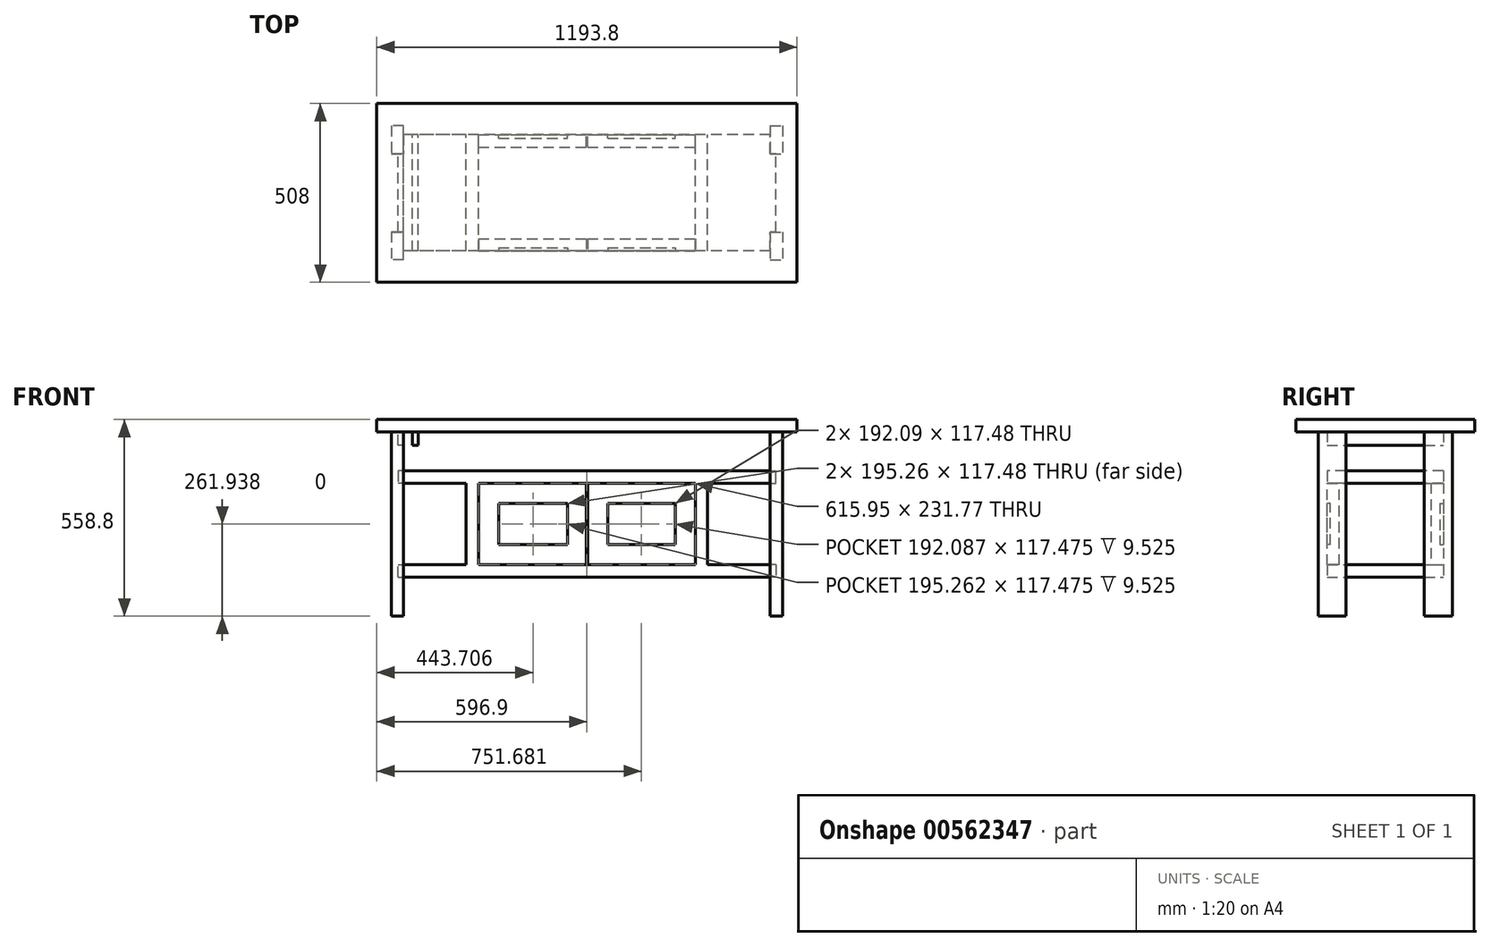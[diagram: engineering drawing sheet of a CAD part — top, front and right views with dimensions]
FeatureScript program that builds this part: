
annotation { "Feature Type Name" : "Feature", "Feature Type Description" : "" }
export const myFeature = defineFeature(function(context is Context, id is Id, definition is map)
    precondition{}
    {
        {
            var Q0;
            Q0=qCreatedBy(makeId("Front.planeOp"),FACE);
            var sketch = newSketch(context, id + "F0", { "sketchPlane" : qUnion([Q0])});
            skLineSegment(sketch, "E0.bottom", {"start": v(596.9, 558.8) * mm, "end": v(-596.9, 558.8) * mm});
            skLineSegment(sketch, "E0.top", {"start": v(596.9, 523.88) * mm, "end": v(-596.9, 523.88) * mm});
            skLineSegment(sketch, "E0.left", {"start": v(596.9, 558.8) * mm, "end": v(596.9, 523.88) * mm});
            skLineSegment(sketch, "E0.right", {"start": v(-596.9, 558.8) * mm, "end": v(-596.9, 523.88) * mm});
            skPoint(sketch, "E0.middle", {"position": v(0, 541.34) * mm});
            skLineSegment(sketch, "E1.bottom", {"start": v(536.58, 146.05) * mm, "end": v(342.9, 146.05) * mm});
            skLineSegment(sketch, "E1.top", {"start": v(536.58, 111.13) * mm, "end": v(-536.58, 111.12) * mm});
            skLineSegment(sketch, "E1.left", {"start": v(536.58, 146.05) * mm, "end": v(536.58, 111.13) * mm});
            skLineSegment(sketch, "E1.right", {"start": v(-536.58, 146.05) * mm, "end": v(-536.58, 111.12) * mm});
            skPoint(sketch, "E1.middle", {"position": v(0, 128.59) * mm});
            skLineSegment(sketch, "E2", {"start": v(307.98, 146.05) * mm, "end": v(307.98, 377.83) * mm});
            skLineSegment(sketch, "E3", {"start": v(342.9, 377.82) * mm, "end": v(342.9, 146.05) * mm});
            skLineSegment(sketch, "E4", {"start": v(0, 0) * mm, "end": v(0, -191.79) * mm, "construction": true});
            skLineSegment(sketch, "E5.MirrorCS", {"start": v(-342.9, 377.82) * mm, "end": v(-342.9, 146.05) * mm});
            skLineSegment(sketch, "E6.MirrorCS", {"start": v(-307.98, 146.05) * mm, "end": v(-307.98, 377.83) * mm});
            skLineSegment(sketch, "E7.trimOffspring", {"start": v(307.98, 146.05) * mm, "end": v(-307.98, 146.05) * mm});
            skLineSegment(sketch, "E8.trimOffspring", {"start": v(-342.9, 146.05) * mm, "end": v(-536.58, 146.05) * mm});
            skLineSegment(sketch, "E9.bottom", {"start": v(-536.58, 377.83) * mm, "end": v(-342.9, 377.83) * mm});
            skLineSegment(sketch, "E9.top", {"start": v(-536.58, 412.75) * mm, "end": v(536.57, 412.75) * mm});
            skLineSegment(sketch, "E9.left", {"start": v(-536.58, 377.83) * mm, "end": v(-536.58, 412.75) * mm});
            skLineSegment(sketch, "E9.right", {"start": v(536.58, 377.83) * mm, "end": v(536.58, 412.75) * mm});
            skLineSegment(sketch, "E10.trimOffspring", {"start": v(-307.98, 377.83) * mm, "end": v(307.97, 377.83) * mm});
            skLineSegment(sketch, "E11.trimOffspring", {"start": v(342.9, 377.83) * mm, "end": v(536.57, 377.83) * mm});
            skLineSegment(sketch, "E12", {"start": v(-342.9, 377.83) * mm, "end": v(-307.98, 377.83) * mm, "construction": true});
            skLineSegment(sketch, "E13.bottom", {"start": v(536.57, 523.88) * mm, "end": v(520.7, 523.88) * mm});
            skLineSegment(sketch, "E13.top", {"start": v(536.57, 485.78) * mm, "end": v(520.7, 485.78) * mm});
            skLineSegment(sketch, "E13.left", {"start": v(536.57, 523.88) * mm, "end": v(536.57, 485.78) * mm});
            skLineSegment(sketch, "E13.right", {"start": v(520.7, 523.88) * mm, "end": v(520.7, 485.78) * mm});
            skLineSegment(sketch, "E14.bottom", {"start": v(495.3, 523.88) * mm, "end": v(479.43, 523.88) * mm});
            skLineSegment(sketch, "E14.top", {"start": v(495.3, 485.78) * mm, "end": v(479.43, 485.78) * mm});
            skLineSegment(sketch, "E14.left", {"start": v(495.3, 523.88) * mm, "end": v(495.3, 485.78) * mm});
            skLineSegment(sketch, "E14.right", {"start": v(479.43, 523.88) * mm, "end": v(479.43, 485.78) * mm});
            skLineSegment(sketch, "E15.MirrorCS", {"start": v(-520.7, 523.88) * mm, "end": v(-520.7, 485.77) * mm});
            skLineSegment(sketch, "E16.MirrorCS", {"start": v(-495.3, 485.78) * mm, "end": v(-479.43, 485.78) * mm});
            skLineSegment(sketch, "E17.MirrorCS", {"start": v(-536.58, 485.77) * mm, "end": v(-520.7, 485.77) * mm});
            skLineSegment(sketch, "E18.MirrorCS", {"start": v(-495.3, 523.88) * mm, "end": v(-495.3, 485.77) * mm});
            skLineSegment(sketch, "E19.MirrorCS", {"start": v(-479.43, 523.88) * mm, "end": v(-479.43, 485.77) * mm});
            skLineSegment(sketch, "E20.MirrorCS", {"start": v(-536.57, 523.88) * mm, "end": v(-520.7, 523.88) * mm});
            skLineSegment(sketch, "E21.MirrorCS", {"start": v(-536.57, 523.88) * mm, "end": v(-536.57, 485.77) * mm});
            skLineSegment(sketch, "E22.MirrorCS", {"start": v(-495.3, 523.88) * mm, "end": v(-479.43, 523.88) * mm});
            skSolve(sketch);
        }
        {
            var Q0;
            Q0=makeQuery(id+"F0.imprint","IMPRINT",FACE,{"disambiguationData":[TD([[makeQuery(id+"F0.imprint","IMPRINT",EDGE,{"derivedFrom":sQuery(id+"F0.wireOp",EDGE,"E0.bottom")}),1.0]])]});
            extrude(context, id + "F1", {"entities" : qUnion([Q0]), "endBound" : BoundingType.SYMMETRIC, "depth" : 508 * mm, "offsetDistance" : 25.4 * mm});
        }
        {
            var Q0;
            Q0=makeQuery(id+"F0.imprint","IMPRINT",FACE,{"disambiguationData":[TD([[makeQuery(id+"F0.imprint","IMPRINT",EDGE,{"derivedFrom":sQuery(id+"F0.wireOp",EDGE,"E1.bottom")}),1.0]])]});
            var Q1;
            Q1=makeQuery(id+"F0.imprint","IMPRINT",FACE,{"disambiguationData":[TD([[makeQuery(id+"F0.imprint","IMPRINT",EDGE,{"derivedFrom":sQuery(id+"F0.wireOp",EDGE,"E13.bottom")}),1.0]])]});
            var Q2;
            Q2=makeQuery(id+"F0.imprint","IMPRINT",FACE,{"disambiguationData":[TD([[makeQuery(id+"F0.imprint","IMPRINT",EDGE,{"derivedFrom":sQuery(id+"F0.wireOp",EDGE,"E14.bottom")}),1.0]])]});
            var Q3;
            Q3=makeQuery(id+"F0.imprint","IMPRINT",FACE,{"disambiguationData":[TD([[makeQuery(id+"F0.imprint","IMPRINT",EDGE,{"derivedFrom":sQuery(id+"F0.wireOp",EDGE,"E16.MirrorCS")}),1.0]])]});
            var Q4;
            Q4=makeQuery(id+"F0.imprint","IMPRINT",FACE,{"disambiguationData":[TD([[makeQuery(id+"F0.imprint","IMPRINT",EDGE,{"derivedFrom":sQuery(id+"F0.wireOp",EDGE,"E15.MirrorCS")}),-1.0]])]});
            var Q5;
            Q5=makeQuery(id+"F1.opExtrude","CAP_FACE",FACE,{"disambiguationData":[OSD([sQuery(id+"F0.wireOp",EDGE,"E0.bottom"),sQuery(id+"F0.wireOp",EDGE,"E0.top"),sQuery(id+"F0.wireOp",EDGE,"E0.left"),sQuery(id+"F0.wireOp",EDGE,"E0.right"),sQuery(id+"F0.wireOp",EDGE,"VGV9EeQM-khb5-w9n3-FiPv-19kF0ZQjxZJE"),sQuery(id+"F0.wireOp",EDGE,"a7e9f2bc-2c81-4aa9-9757-ab29dbda99602.MirrorCS")])],"isStart":false});
            var Q6;
            Q6=makeQuery(id+"F1.opExtrude","CAP_FACE",FACE,{"disambiguationData":[OSD([sQuery(id+"F0.wireOp",EDGE,"E0.bottom"),sQuery(id+"F0.wireOp",EDGE,"E0.top"),sQuery(id+"F0.wireOp",EDGE,"E0.left"),sQuery(id+"F0.wireOp",EDGE,"E0.right"),sQuery(id+"F0.wireOp",EDGE,"VGV9EeQM-khb5-w9n3-FiPv-19kF0ZQjxZJE"),sQuery(id+"F0.wireOp",EDGE,"a7e9f2bc-2c81-4aa9-9757-ab29dbda99602.MirrorCS")])],"isStart":true});
            extrude(context, id + "F2", {"entities" : qUnion([Q0, Q1, Q2, Q3, Q4]), "endBound" : BoundingType.UP_TO_SURFACE, "depth" : 25.4 * mm, "endBoundEntityFace" : qUnion([Q5]), "hasOffset" : true, "offsetDistance" : 88.9 * mm, "hasSecondDirection" : true, "secondDirectionBound" : SecondDirectionBoundingType.UP_TO_SURFACE, "secondDirectionOppositeDirection" : true, "secondDirectionDepth" : 25.4 * mm, "secondDirectionBoundEntityFace" : qUnion([Q6]), "hasSecondDirectionOffset" : true, "secondDirectionOffsetDistance" : 88.9 * mm});
        }
        {
            var Q0;
            Q0=qCreatedBy(makeId("Top.planeOp"),FACE);
            var sketch = newSketch(context, id + "F3", { "sketchPlane" : qUnion([Q0])});
            skLineSegment(sketch, "E23", {"start": v(0, -153.77) * mm, "end": v(0, 0) * mm, "construction": true});
            skLineSegment(sketch, "E24.bottom", {"start": v(-555.63, 111.13) * mm, "end": v(-520.7, 111.13) * mm});
            skLineSegment(sketch, "E24.top", {"start": v(-555.63, 190.5) * mm, "end": v(-520.7, 190.5) * mm});
            skLineSegment(sketch, "E24.left", {"start": v(-555.62, 111.13) * mm, "end": v(-555.63, 190.5) * mm});
            skLineSegment(sketch, "E24.right", {"start": v(-520.7, 111.13) * mm, "end": v(-520.7, 190.5) * mm});
            skLineSegment(sketch, "E25.bottom", {"start": v(-555.63, -190.5) * mm, "end": v(-520.7, -190.5) * mm});
            skLineSegment(sketch, "E25.top", {"start": v(-555.63, -111.12) * mm, "end": v(-520.7, -111.12) * mm});
            skLineSegment(sketch, "E25.left", {"start": v(-555.62, -190.5) * mm, "end": v(-555.62, -111.12) * mm});
            skLineSegment(sketch, "E25.right", {"start": v(-520.7, -190.5) * mm, "end": v(-520.7, -111.13) * mm});
            skLineSegment(sketch, "E26.MirrorCS", {"start": v(520.7, -190.5) * mm, "end": v(520.7, -111.13) * mm});
            skLineSegment(sketch, "E27.MirrorCS", {"start": v(555.62, -190.5) * mm, "end": v(555.62, -111.13) * mm});
            skLineSegment(sketch, "E28.MirrorCS", {"start": v(555.63, 111.13) * mm, "end": v(520.7, 111.13) * mm});
            skLineSegment(sketch, "E29.MirrorCS", {"start": v(555.63, 190.5) * mm, "end": v(520.7, 190.5) * mm});
            skLineSegment(sketch, "E30.MirrorCS", {"start": v(555.62, 111.13) * mm, "end": v(555.62, 190.5) * mm});
            skLineSegment(sketch, "E31.MirrorCS", {"start": v(520.7, 111.13) * mm, "end": v(520.7, 190.5) * mm});
            skLineSegment(sketch, "E32.MirrorCS", {"start": v(555.62, -111.12) * mm, "end": v(520.7, -111.12) * mm});
            skLineSegment(sketch, "E33.MirrorCS", {"start": v(555.62, -190.5) * mm, "end": v(520.7, -190.5) * mm});
            skSolve(sketch);
        }
        {
            var Q0;
            Q0 = qSketchRegion(id + "F3", true);
            var Q1;
            Q1=makeQuery(id+"F1.opExtrude","SWEPT_FACE",FACE,{"disambiguationData":[OSD([sQuery(id+"F0.wireOp",EDGE,"E0.top"),sQuery(id+"F0.wireOp",EDGE,"VGV9EeQM-khb5-w9n3-FiPv-19kF0ZQjxZJE"),sQuery(id+"F0.wireOp",EDGE,"a7e9f2bc-2c81-4aa9-9757-ab29dbda99602.MirrorCS")])]});
            extrude(context, id + "F4", {"entities" : qUnion([Q0]), "operationType" : NewBodyOperationType.ADD, "endBound" : BoundingType.UP_TO_SURFACE, "depth" : 25.4 * mm, "endBoundEntityFace" : qUnion([Q1]), "offsetDistance" : 25.4 * mm});
        }
        {
            var Q0;
            Q0=makeQuery(id+"F2.opExtrude","CAP_FACE",FACE,{"disambiguationData":[OSD([sQuery(id+"F0.wireOp",EDGE,"E0.bottom"),sQuery(id+"F0.wireOp",EDGE,"E0.top"),sQuery(id+"F0.wireOp",EDGE,"E0.left"),sQuery(id+"F0.wireOp",EDGE,"E0.right"),sQuery(id+"F0.wireOp",EDGE,"E9.top")])],"isStart":false});
            var sketch = newSketch(context, id + "F5", { "sketchPlane" : qUnion([Q0])});
            skLineSegment(sketch, "E34.bottom", {"start": v(-307.98, 377.83) * mm, "end": v(-1.59, 377.83) * mm});
            skLineSegment(sketch, "E34.top", {"start": v(-307.98, 146.05) * mm, "end": v(-1.59, 146.05) * mm});
            skLineSegment(sketch, "E34.left", {"start": v(-307.98, 377.83) * mm, "end": v(-307.98, 146.05) * mm});
            skLineSegment(sketch, "E34.right", {"start": v(-1.59, 377.83) * mm, "end": v(-1.59, 146.05) * mm});
            skLineSegment(sketch, "E35.bottom", {"start": v(1.59, 146.05) * mm, "end": v(307.98, 146.05) * mm});
            skLineSegment(sketch, "E35.top", {"start": v(1.59, 377.83) * mm, "end": v(307.98, 377.83) * mm});
            skLineSegment(sketch, "E35.left", {"start": v(1.59, 146.05) * mm, "end": v(1.59, 377.83) * mm});
            skLineSegment(sketch, "E35.right", {"start": v(307.98, 146.05) * mm, "end": v(307.98, 377.83) * mm});
            skLineSegment(sketch, "E36.0", {"start": v(-250.83, 320.68) * mm, "end": v(-55.56, 320.68) * mm});
            skLineSegment(sketch, "E36.1", {"start": v(-250.83, 320.68) * mm, "end": v(-250.83, 203.2) * mm});
            skLineSegment(sketch, "E36.2", {"start": v(-250.83, 203.2) * mm, "end": v(-55.56, 203.2) * mm});
            skLineSegment(sketch, "E36.3", {"start": v(-55.56, 203.2) * mm, "end": v(-55.56, 320.68) * mm});
            skLineSegment(sketch, "E37.0", {"start": v(58.74, 320.68) * mm, "end": v(250.83, 320.68) * mm});
            skLineSegment(sketch, "E37.1", {"start": v(58.74, 203.2) * mm, "end": v(58.74, 320.68) * mm});
            skLineSegment(sketch, "E37.2", {"start": v(58.74, 203.2) * mm, "end": v(250.82, 203.2) * mm});
            skLineSegment(sketch, "E37.3", {"start": v(250.83, 203.2) * mm, "end": v(250.83, 320.68) * mm});
            skPoint(sketch, "E38", {"position": v(-86.42, 145.11) * mm});
            skSolve(sketch);
        }
        {
            var Q0;
            Q0 = qSketchRegion(id + "F5", true);
            var Q1;
            Q1=makeQuery(id+"F5.imprint","IMPRINT",FACE,{"disambiguationData":[TD([[makeQuery(id+"F5.imprint","IMPRINT",EDGE,{"derivedFrom":sQuery(id+"F5.wireOp",EDGE,"E36.0")}),-1.0]])]});
            var Q2;
            Q2=makeQuery(id+"F5.imprint","IMPRINT",FACE,{"disambiguationData":[TD([[makeQuery(id+"F5.imprint","IMPRINT",EDGE,{"derivedFrom":sQuery(id+"F5.wireOp",EDGE,"E37.0")}),-1.0]])]});
            extrude(context, id + "F6", {"entities" : qUnion([Q0, Q1, Q2]), "oppositeDirection" : true, "depth" : 34.92 * mm, "offsetDistance" : 25.4 * mm});
        }
        {
            var Q0;
            Q0=makeQuery(id+"F5.imprint","IMPRINT",FACE,{"disambiguationData":[TD([[makeQuery(id+"F5.imprint","IMPRINT",EDGE,{"derivedFrom":sQuery(id+"F5.wireOp",EDGE,"E36.0")}),-1.0]])]});
            var Q1;
            Q1=makeQuery(id+"F5.imprint","IMPRINT",FACE,{"disambiguationData":[TD([[makeQuery(id+"F5.imprint","IMPRINT",EDGE,{"derivedFrom":sQuery(id+"F5.wireOp",EDGE,"E37.0")}),-1.0]])]});
            extrude(context, id + "F7", {"entities" : qUnion([Q0, Q1]), "operationType" : NewBodyOperationType.REMOVE, "oppositeDirection" : true, "depth" : 9.52 * mm, "offsetDistance" : 25.4 * mm});
        }
        {
            var Q0;
            Q0=makeQuery(id+"F6.opExtrude","SWEPT_BODY",BODY,{"disambiguationData":[OSD([sQuery(id+"F5.wireOp",EDGE,"E34.bottom"),sQuery(id+"F5.wireOp",EDGE,"E34.top"),sQuery(id+"F5.wireOp",EDGE,"E34.left"),sQuery(id+"F5.wireOp",EDGE,"E34.right")])]});
            var Q1;
            Q1=makeQuery(id+"F6.opExtrude","SWEPT_BODY",BODY,{"disambiguationData":[OSD([sQuery(id+"F5.wireOp",EDGE,"E35.bottom"),sQuery(id+"F5.wireOp",EDGE,"E35.top"),sQuery(id+"F5.wireOp",EDGE,"E35.left"),sQuery(id+"F5.wireOp",EDGE,"E35.right")])]});
            var Q2;
            Q2=qCreatedBy(makeId("Front.planeOp"),FACE);
            mirror(context, id + "F8", {"entities" : qUnion([Q0, Q1]), "mirrorPlane" : qUnion([Q2])});
        }
    });
